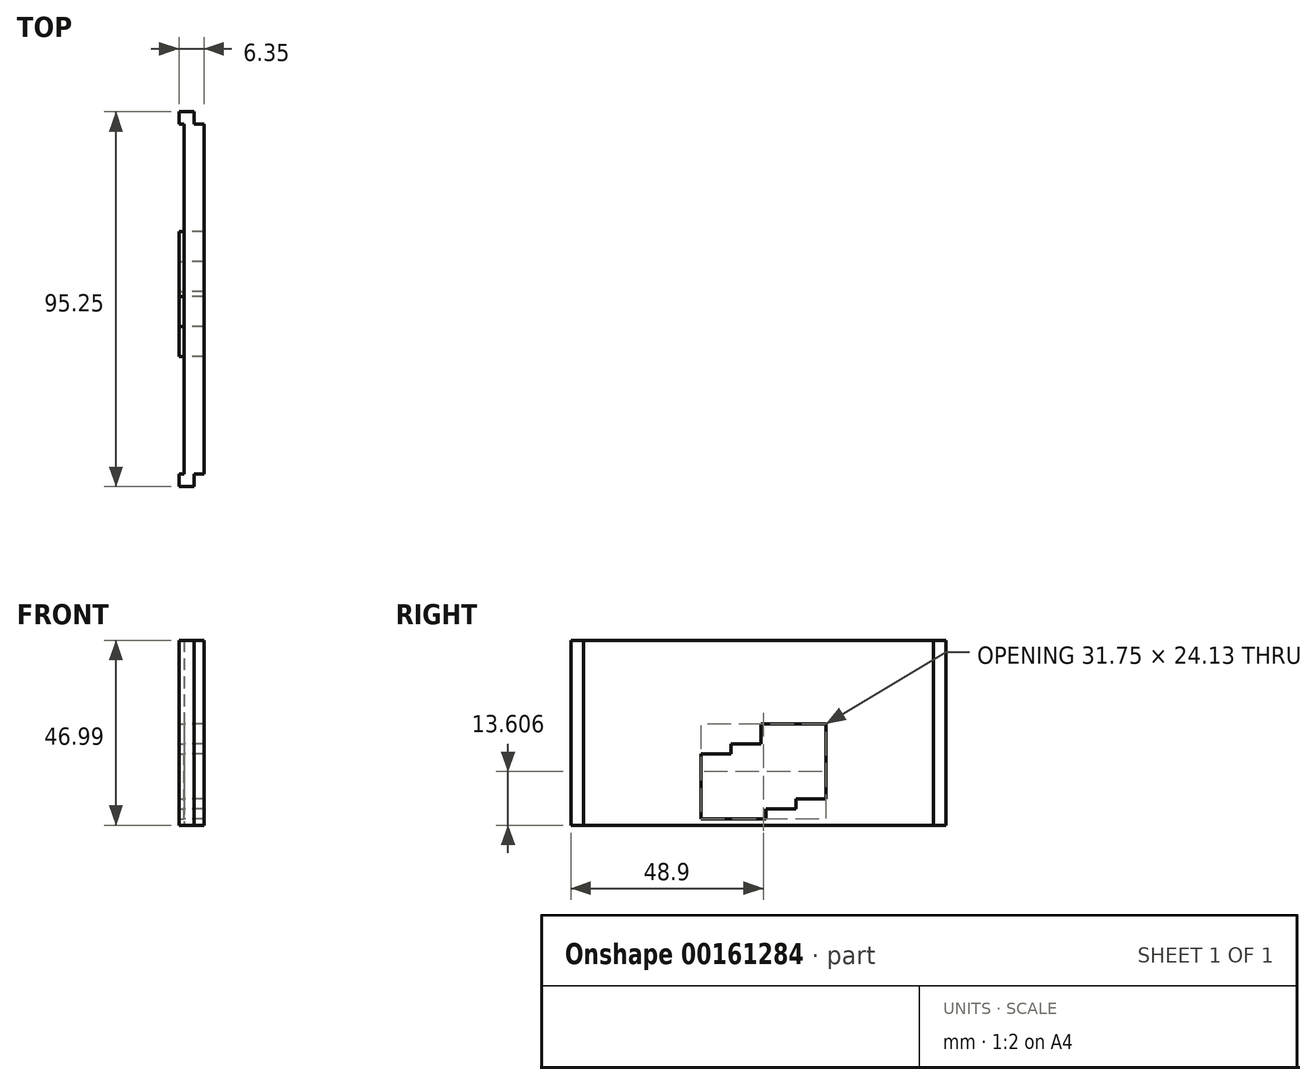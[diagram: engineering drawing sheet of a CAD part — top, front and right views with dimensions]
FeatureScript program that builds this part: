
annotation { "Feature Type Name" : "Feature", "Feature Type Description" : "" }
export const myFeature = defineFeature(function(context is Context, id is Id, definition is map)
    precondition{}
    {
        {
            var Q0;
            Q0=qCreatedBy(makeId("Right.planeOp"),FACE);
            var sketch = newSketch(context, id + "F0", { "sketchPlane" : qUnion([Q0])});
            skLineSegment(sketch, "E0.bottom", {"start": v(-51.44, 23.45) * mm, "end": v(43.81, 23.45) * mm});
            skLineSegment(sketch, "E0.top", {"start": v(-51.44, -23.54) * mm, "end": v(43.81, -23.54) * mm});
            skLineSegment(sketch, "E0.left", {"start": v(-51.44, 23.45) * mm, "end": v(-51.44, -23.54) * mm});
            skLineSegment(sketch, "E0.right", {"start": v(43.81, 23.45) * mm, "end": v(43.81, -23.54) * mm});
            skLineSegment(sketch, "E1", {"start": v(-3.18, 2.13) * mm, "end": v(13.33, 2.13) * mm});
            skLineSegment(sketch, "E2.top", {"start": v(-3.18, -16.92) * mm, "end": v(13.33, -16.92) * mm});
            skLineSegment(sketch, "E2.left", {"start": v(-3.18, 2.13) * mm, "end": v(-3.18, -16.92) * mm});
            skLineSegment(sketch, "E2.right", {"start": v(13.33, 2.13) * mm, "end": v(13.33, -16.92) * mm});
            skLineSegment(sketch, "E3.bottom", {"start": v(-10.8, -2.95) * mm, "end": v(5.71, -2.95) * mm});
            skLineSegment(sketch, "E3.top", {"start": v(-10.8, -19.46) * mm, "end": v(5.71, -19.46) * mm});
            skLineSegment(sketch, "E3.left", {"start": v(-10.8, -2.95) * mm, "end": v(-10.8, -19.46) * mm});
            skLineSegment(sketch, "E3.right", {"start": v(5.71, -2.95) * mm, "end": v(5.71, -19.46) * mm});
            skLineSegment(sketch, "E4", {"start": v(5.71, -19.46) * mm, "end": v(5.71, -22) * mm, "construction": true});
            skLineSegment(sketch, "E5", {"start": v(5.71, -22) * mm, "end": v(-1.9, -22) * mm, "construction": true});
            skLineSegment(sketch, "E6.bottom", {"start": v(-1.9, -22) * mm, "end": v(-18.42, -22) * mm});
            skLineSegment(sketch, "E6.top", {"start": v(-1.9, -5.49) * mm, "end": v(-18.42, -5.49) * mm});
            skLineSegment(sketch, "E6.left", {"start": v(-1.9, -22) * mm, "end": v(-1.9, -5.49) * mm});
            skLineSegment(sketch, "E6.right", {"start": v(-18.42, -22) * mm, "end": v(-18.42, -5.49) * mm});
            skSolve(sketch);
        }
        {
            var Q0;
            Q0=makeQuery(id+"F0.imprint","IMPRINT",FACE,{"disambiguationData":[TD([[makeQuery(id+"F0.imprint","IMPRINT",EDGE,{"derivedFrom":sQuery(id+"F0.wireOp",EDGE,"E0.bottom")}),-1.0]])]});
            extrude(context, id + "F1", {"entities" : qUnion([Q0]), "depth" : 2.54 * mm});
        }
        {
            var Q0;
            Q0=makeQuery(id+"F1.opExtrude","CAP_FACE",FACE,{"disambiguationData":[OSD([sQuery(id+"F0.wireOp",EDGE,"E0.bottom"),sQuery(id+"F0.wireOp",EDGE,"E0.top"),sQuery(id+"F0.wireOp",EDGE,"E0.left"),sQuery(id+"F0.wireOp",EDGE,"E0.right"),sQuery(id+"F0.wireOp",EDGE,"6dFb7bQy-Tsit-ki43-gD21-n3580RZvwL36.top"),sQuery(id+"F0.wireOp",EDGE,"6dFb7bQy-Tsit-ki43-gD21-n3580RZvwL36.left"),sQuery(id+"F0.wireOp",EDGE,"6dFb7bQy-Tsit-ki43-gD21-n3580RZvwL36.right"),sQuery(id+"F0.wireOp",EDGE,"30b0265e-30c0-49d3-83b3-d44f5d3d6c73.bottom"),sQuery(id+"F0.wireOp",EDGE,"30b0265e-30c0-49d3-83b3-d44f5d3d6c73.right"),sQuery(id+"F0.wireOp",EDGE,"SF6fetFu-4xI5-y6nI-tUDN-0U6HBoudLmk6.bottom"),sQuery(id+"F0.wireOp",EDGE,"SF6fetFu-4xI5-y6nI-tUDN-0U6HBoudLmk6.top"),sQuery(id+"F0.wireOp",EDGE,"SF6fetFu-4xI5-y6nI-tUDN-0U6HBoudLmk6.left"),sQuery(id+"F0.wireOp",EDGE,"SF6fetFu-4xI5-y6nI-tUDN-0U6HBoudLmk6.right"),sQuery(id+"F0.wireOp",EDGE,"Eo5iXCAk-CxUs-Plu0-i23o-LOiFup1MPPJV.bottom"),sQuery(id+"F0.wireOp",EDGE,"Eo5iXCAk-CxUs-Plu0-i23o-LOiFup1MPPJV.top"),sQuery(id+"F0.wireOp",EDGE,"Eo5iXCAk-CxUs-Plu0-i23o-LOiFup1MPPJV.left"),sQuery(id+"F0.wireOp",EDGE,"Eo5iXCAk-CxUs-Plu0-i23o-LOiFup1MPPJV.right")])],"isStart":false});
            var sketch = newSketch(context, id + "F2", { "sketchPlane" : qUnion([Q0])});
            skLineSegment(sketch, "E7.bottom", {"start": v(-51.44, 23.45) * mm, "end": v(-48.26, 23.45) * mm});
            skLineSegment(sketch, "E7.top", {"start": v(-51.44, -23.54) * mm, "end": v(-48.26, -23.54) * mm});
            skLineSegment(sketch, "E7.left", {"start": v(-51.44, 23.45) * mm, "end": v(-51.44, -23.54) * mm});
            skLineSegment(sketch, "E7.right", {"start": v(-48.26, 23.45) * mm, "end": v(-48.26, -23.54) * mm});
            skLineSegment(sketch, "E8.bottom", {"start": v(43.81, 23.45) * mm, "end": v(40.64, 23.45) * mm});
            skLineSegment(sketch, "E8.top", {"start": v(43.81, -23.54) * mm, "end": v(40.64, -23.54) * mm});
            skLineSegment(sketch, "E8.left", {"start": v(43.81, 23.45) * mm, "end": v(43.81, -23.54) * mm});
            skLineSegment(sketch, "E8.right", {"start": v(40.64, 23.45) * mm, "end": v(40.64, -23.54) * mm});
            skLineSegment(sketch, "E9.bottom", {"start": v(-48.26, 23.45) * mm, "end": v(40.64, 23.45) * mm});
            skLineSegment(sketch, "E9.top", {"start": v(-48.26, -23.54) * mm, "end": v(40.64, -23.54) * mm});
            skSolve(sketch);
        }
        {
            var Q0;
            Q0=makeQuery(id+"F2.imprint","IMPRINT",FACE,{"disambiguationData":[TD([[makeQuery(id+"F2.imprint","IMPRINT",EDGE,{"derivedFrom":sQuery(id+"F2.wireOp",EDGE,"E9.bottom")}),-1.0]])]});
            extrude(context, id + "F3", {"entities" : qUnion([Q0]), "operationType" : NewBodyOperationType.ADD, "depth" : 2.54 * mm});
        }
        {
            var Q0;
            Q0=makeQuery(id+"F1.opExtrude","CAP_FACE",FACE,{"disambiguationData":[OSD([sQuery(id+"F0.wireOp",EDGE,"E0.bottom"),sQuery(id+"F0.wireOp",EDGE,"E0.top"),sQuery(id+"F0.wireOp",EDGE,"E0.left"),sQuery(id+"F0.wireOp",EDGE,"E0.right"),sQuery(id+"F0.wireOp",EDGE,"6dFb7bQy-Tsit-ki43-gD21-n3580RZvwL36.top"),sQuery(id+"F0.wireOp",EDGE,"6dFb7bQy-Tsit-ki43-gD21-n3580RZvwL36.left"),sQuery(id+"F0.wireOp",EDGE,"6dFb7bQy-Tsit-ki43-gD21-n3580RZvwL36.right"),sQuery(id+"F0.wireOp",EDGE,"30b0265e-30c0-49d3-83b3-d44f5d3d6c73.bottom"),sQuery(id+"F0.wireOp",EDGE,"30b0265e-30c0-49d3-83b3-d44f5d3d6c73.right"),sQuery(id+"F0.wireOp",EDGE,"SF6fetFu-4xI5-y6nI-tUDN-0U6HBoudLmk6.bottom"),sQuery(id+"F0.wireOp",EDGE,"SF6fetFu-4xI5-y6nI-tUDN-0U6HBoudLmk6.top"),sQuery(id+"F0.wireOp",EDGE,"SF6fetFu-4xI5-y6nI-tUDN-0U6HBoudLmk6.left"),sQuery(id+"F0.wireOp",EDGE,"SF6fetFu-4xI5-y6nI-tUDN-0U6HBoudLmk6.right"),sQuery(id+"F0.wireOp",EDGE,"Eo5iXCAk-CxUs-Plu0-i23o-LOiFup1MPPJV.bottom"),sQuery(id+"F0.wireOp",EDGE,"Eo5iXCAk-CxUs-Plu0-i23o-LOiFup1MPPJV.top"),sQuery(id+"F0.wireOp",EDGE,"Eo5iXCAk-CxUs-Plu0-i23o-LOiFup1MPPJV.left"),sQuery(id+"F0.wireOp",EDGE,"Eo5iXCAk-CxUs-Plu0-i23o-LOiFup1MPPJV.right")])],"isStart":true});
            var sketch = newSketch(context, id + "F4", { "sketchPlane" : qUnion([Q0])});
            skLineSegment(sketch, "E10.bottom", {"start": v(-43.81, 23.45) * mm, "end": v(51.44, 23.45) * mm});
            skLineSegment(sketch, "E10.top", {"start": v(-43.81, -23.54) * mm, "end": v(51.44, -23.54) * mm});
            skLineSegment(sketch, "E10.left", {"start": v(-43.81, 23.45) * mm, "end": v(-43.81, -23.54) * mm});
            skLineSegment(sketch, "E10.right", {"start": v(51.44, 23.45) * mm, "end": v(51.44, -23.54) * mm});
            skLineSegment(sketch, "E11.bottom", {"start": v(-43.81, 23.45) * mm, "end": v(-40.64, 23.45) * mm});
            skLineSegment(sketch, "E11.top", {"start": v(-43.81, -23.54) * mm, "end": v(-40.64, -23.54) * mm});
            skLineSegment(sketch, "E11.right", {"start": v(-40.64, 23.45) * mm, "end": v(-40.64, -23.54) * mm});
            skLineSegment(sketch, "E12.bottom", {"start": v(51.44, -23.54) * mm, "end": v(48.26, -23.54) * mm});
            skLineSegment(sketch, "E12.top", {"start": v(51.44, 23.45) * mm, "end": v(48.26, 23.45) * mm});
            skLineSegment(sketch, "E12.left", {"start": v(51.44, -23.54) * mm, "end": v(51.44, 23.45) * mm});
            skLineSegment(sketch, "E12.right", {"start": v(48.26, -23.54) * mm, "end": v(48.26, 23.45) * mm});
            skSolve(sketch);
        }
        {
            var Q0;
            Q0=makeQuery(id+"F4.imprint","IMPRINT",FACE,{"disambiguationData":[TD([[makeQuery(id+"F4.imprint","IMPRINT",EDGE,{"derivedFrom":sQuery(id+"F4.wireOp",EDGE,"E10.bottom")}),1.0]])]});
            var Q1;
            Q1=makeQuery(id+"F4.imprint","IMPRINT",FACE,{"disambiguationData":[TD([[makeQuery(id+"F4.imprint","IMPRINT",EDGE,{"derivedFrom":makeQuery(id+"F1.opExtrude","CAP_EDGE",EDGE,{"disambiguationData":[OSD([sQuery(id+"F0.wireOp",EDGE,"E1")])],"isStart":true})}),1.0]])]});
            extrude(context, id + "F5", {"entities" : qUnion([Q0, Q1]), "operationType" : NewBodyOperationType.ADD, "depth" : 1.27 * mm});
        }
    });
